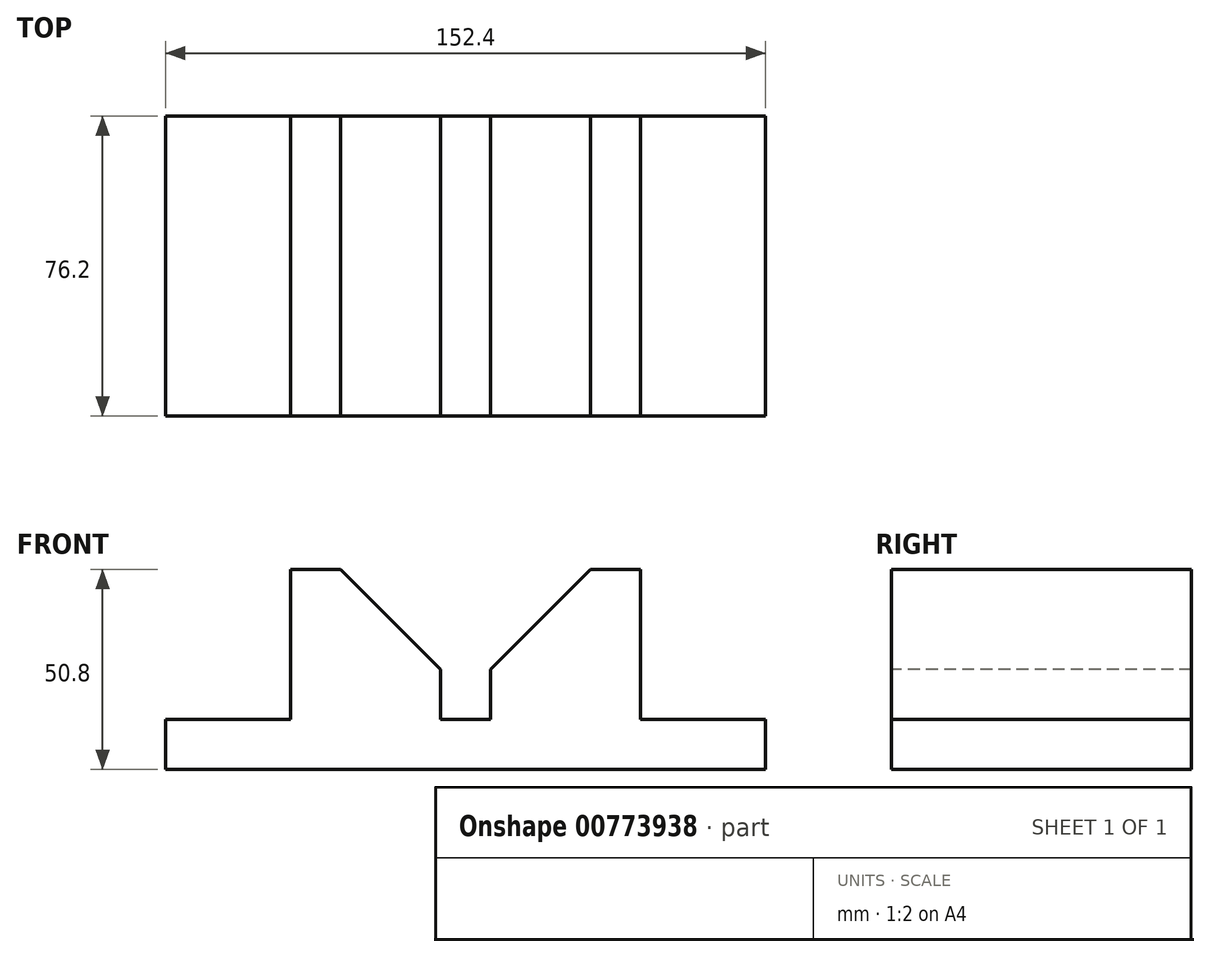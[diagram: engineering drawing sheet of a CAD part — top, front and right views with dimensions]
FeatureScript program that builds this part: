
annotation { "Feature Type Name" : "Feature", "Feature Type Description" : "" }
export const myFeature = defineFeature(function(context is Context, id is Id, definition is map)
    precondition{}
    {
        {
            var Q0;
            Q0=qCreatedBy(makeId("Front.planeOp"),FACE);
            var sketch = newSketch(context, id + "F0", { "sketchPlane" : qUnion([Q0])});
            skLineSegment(sketch, "E0", {"start": v(0, 0) * mm, "end": v(152.4, 0) * mm});
            skLineSegment(sketch, "E1", {"start": v(152.4, 0) * mm, "end": v(152.4, 50.8) * mm});
            skLineSegment(sketch, "E2", {"start": v(152.4, 50.8) * mm, "end": v(0, 50.8) * mm});
            skLineSegment(sketch, "E3", {"start": v(0, 50.8) * mm, "end": v(0, 0) * mm});
            skSolve(sketch);
        }
        {
            var Q0;
            Q0=makeQuery(id+"F0.imprint","IMPRINT",FACE,{"disambiguationData":[TD([[makeQuery(id+"F0.imprint","IMPRINT",EDGE,{"derivedFrom":sQuery(id+"F0.wireOp",EDGE,"E0")}),1.0]])]});
            extrude(context, id + "F1", {"entities" : qUnion([Q0]), "depth" : 76.2 * mm, "offsetDistance" : 25.4 * mm});
        }
        {
            var Q0;
            Q0=makeQuery(id+"F1.opExtrude","CAP_FACE",FACE,{"disambiguationData":[OSD([sQuery(id+"F0.wireOp",EDGE,"E0"),sQuery(id+"F0.wireOp",EDGE,"E1"),sQuery(id+"F0.wireOp",EDGE,"E2"),sQuery(id+"F0.wireOp",EDGE,"E3")])],"isStart":false});
            var sketch = newSketch(context, id + "F2", { "sketchPlane" : qUnion([Q0])});
            skLineSegment(sketch, "E4", {"start": v(152.4, 50.8) * mm, "end": v(152.4, 12.7) * mm});
            skLineSegment(sketch, "E5", {"start": v(152.4, 12.7) * mm, "end": v(120.65, 12.7) * mm});
            skLineSegment(sketch, "E6", {"start": v(120.65, 12.7) * mm, "end": v(120.65, 50.8) * mm});
            skLineSegment(sketch, "E7", {"start": v(120.65, 50.8) * mm, "end": v(152.4, 50.8) * mm});
            skSolve(sketch);
        }
        {
            var Q0;
            Q0=makeQuery(id+"F2.imprint","IMPRINT",FACE,{"disambiguationData":[TD([[makeQuery(id+"F2.imprint","IMPRINT",EDGE,{"derivedFrom":sQuery(id+"F2.wireOp",EDGE,"E4")}),1.0]])]});
            extrude(context, id + "F3", {"entities" : qUnion([Q0]), "operationType" : NewBodyOperationType.REMOVE, "oppositeDirection" : true, "depth" : 76.2 * mm, "offsetDistance" : 25.4 * mm});
        }
        {
            var Q0;
            Q0=makeQuery(id+"F1.opExtrude","CAP_FACE",FACE,{"disambiguationData":[OSD([sQuery(id+"F0.wireOp",EDGE,"E0"),sQuery(id+"F0.wireOp",EDGE,"E1"),sQuery(id+"F0.wireOp",EDGE,"E2"),sQuery(id+"F0.wireOp",EDGE,"E3")])],"isStart":false});
            var sketch = newSketch(context, id + "F4", { "sketchPlane" : qUnion([Q0])});
            skLineSegment(sketch, "E8", {"start": v(0, 50.8) * mm, "end": v(0, 12.7) * mm});
            skLineSegment(sketch, "E9", {"start": v(0, 12.7) * mm, "end": v(31.75, 12.7) * mm});
            skLineSegment(sketch, "E10", {"start": v(31.75, 12.7) * mm, "end": v(31.75, 50.8) * mm});
            skLineSegment(sketch, "E11", {"start": v(31.75, 50.8) * mm, "end": v(0, 50.8) * mm});
            skSolve(sketch);
        }
        {
            var Q0;
            Q0=makeQuery(id+"F4.imprint","IMPRINT",FACE,{"disambiguationData":[TD([[makeQuery(id+"F4.imprint","IMPRINT",EDGE,{"derivedFrom":sQuery(id+"F4.wireOp",EDGE,"E8")}),1.0]])]});
            extrude(context, id + "F5", {"entities" : qUnion([Q0]), "operationType" : NewBodyOperationType.REMOVE, "oppositeDirection" : true, "depth" : 76.2 * mm, "offsetDistance" : 25.4 * mm});
        }
        {
            var Q0;
            Q0=makeQuery(id+"F1.opExtrude","CAP_FACE",FACE,{"disambiguationData":[OSD([sQuery(id+"F0.wireOp",EDGE,"E0"),sQuery(id+"F0.wireOp",EDGE,"E1"),sQuery(id+"F0.wireOp",EDGE,"E2"),sQuery(id+"F0.wireOp",EDGE,"E3")])],"isStart":false});
            var sketch = newSketch(context, id + "F6", { "sketchPlane" : qUnion([Q0])});
            skLineSegment(sketch, "E12", {"start": v(69.85, 12.7) * mm, "end": v(82.55, 12.7) * mm});
            skLineSegment(sketch, "E13", {"start": v(82.55, 12.7) * mm, "end": v(82.55, 50.8) * mm});
            skLineSegment(sketch, "E14", {"start": v(69.85, 12.7) * mm, "end": v(69.85, 50.8) * mm});
            skLineSegment(sketch, "E15", {"start": v(69.85, 50.8) * mm, "end": v(82.55, 50.8) * mm});
            skSolve(sketch);
        }
        {
            var Q0;
            Q0=makeQuery(id+"F6.imprint","IMPRINT",FACE,{"disambiguationData":[TD([[makeQuery(id+"F6.imprint","IMPRINT",EDGE,{"derivedFrom":sQuery(id+"F6.wireOp",EDGE,"E12")}),1.0]])]});
            extrude(context, id + "F7", {"entities" : qUnion([Q0]), "operationType" : NewBodyOperationType.REMOVE, "oppositeDirection" : true, "depth" : 76.2 * mm, "offsetDistance" : 25.4 * mm});
        }
        {
            var Q0;
            Q0=makeQuery(id+"F1.opExtrude","CAP_FACE",FACE,{"disambiguationData":[OSD([sQuery(id+"F0.wireOp",EDGE,"E0"),sQuery(id+"F0.wireOp",EDGE,"E1"),sQuery(id+"F0.wireOp",EDGE,"E2"),sQuery(id+"F0.wireOp",EDGE,"E3")])],"isStart":false});
            var sketch = newSketch(context, id + "F8", { "sketchPlane" : qUnion([Q0])});
            skLineSegment(sketch, "E16", {"start": v(107.95, 50.8) * mm, "end": v(82.55, 25.4) * mm});
            skLineSegment(sketch, "E17", {"start": v(82.55, 50.8) * mm, "end": v(107.95, 50.8) * mm});
            skSolve(sketch);
        }
        {
            var Q0;
            {var subQ0=sQuery(id+"F8.wireOp",EDGE,"E16");Q0=makeQuery(id+"F8.imprint","IMPRINT",FACE,{"disambiguationData":[TD([[makeQuery(id+"F8.imprint","IMPRINT",EDGE,{"derivedFrom":subQ0}),-1.0]])]});}
            extrude(context, id + "F9", {"entities" : qUnion([Q0]), "operationType" : NewBodyOperationType.REMOVE, "oppositeDirection" : true, "depth" : 76.2 * mm, "offsetDistance" : 25.4 * mm});
        }
        {
            var Q0;
            Q0=makeQuery(id+"F1.opExtrude","CAP_FACE",FACE,{"disambiguationData":[OSD([sQuery(id+"F0.wireOp",EDGE,"E0"),sQuery(id+"F0.wireOp",EDGE,"E1"),sQuery(id+"F0.wireOp",EDGE,"E2"),sQuery(id+"F0.wireOp",EDGE,"E3")])],"isStart":false});
            var sketch = newSketch(context, id + "F10", { "sketchPlane" : qUnion([Q0])});
            skLineSegment(sketch, "E18", {"start": v(44.45, 50.8) * mm, "end": v(69.85, 25.4) * mm});
            skLineSegment(sketch, "E19", {"start": v(69.85, 50.8) * mm, "end": v(44.45, 50.8) * mm});
            skSolve(sketch);
        }
        {
            var Q0;
            {var subQ0=sQuery(id+"F10.wireOp",EDGE,"E18");Q0=makeQuery(id+"F10.imprint","IMPRINT",FACE,{"disambiguationData":[TD([[makeQuery(id+"F10.imprint","IMPRINT",EDGE,{"derivedFrom":subQ0}),1.0]])]});}
            extrude(context, id + "F11", {"entities" : qUnion([Q0]), "operationType" : NewBodyOperationType.REMOVE, "oppositeDirection" : true, "depth" : 76.2 * mm, "offsetDistance" : 25.4 * mm});
        }
    });
